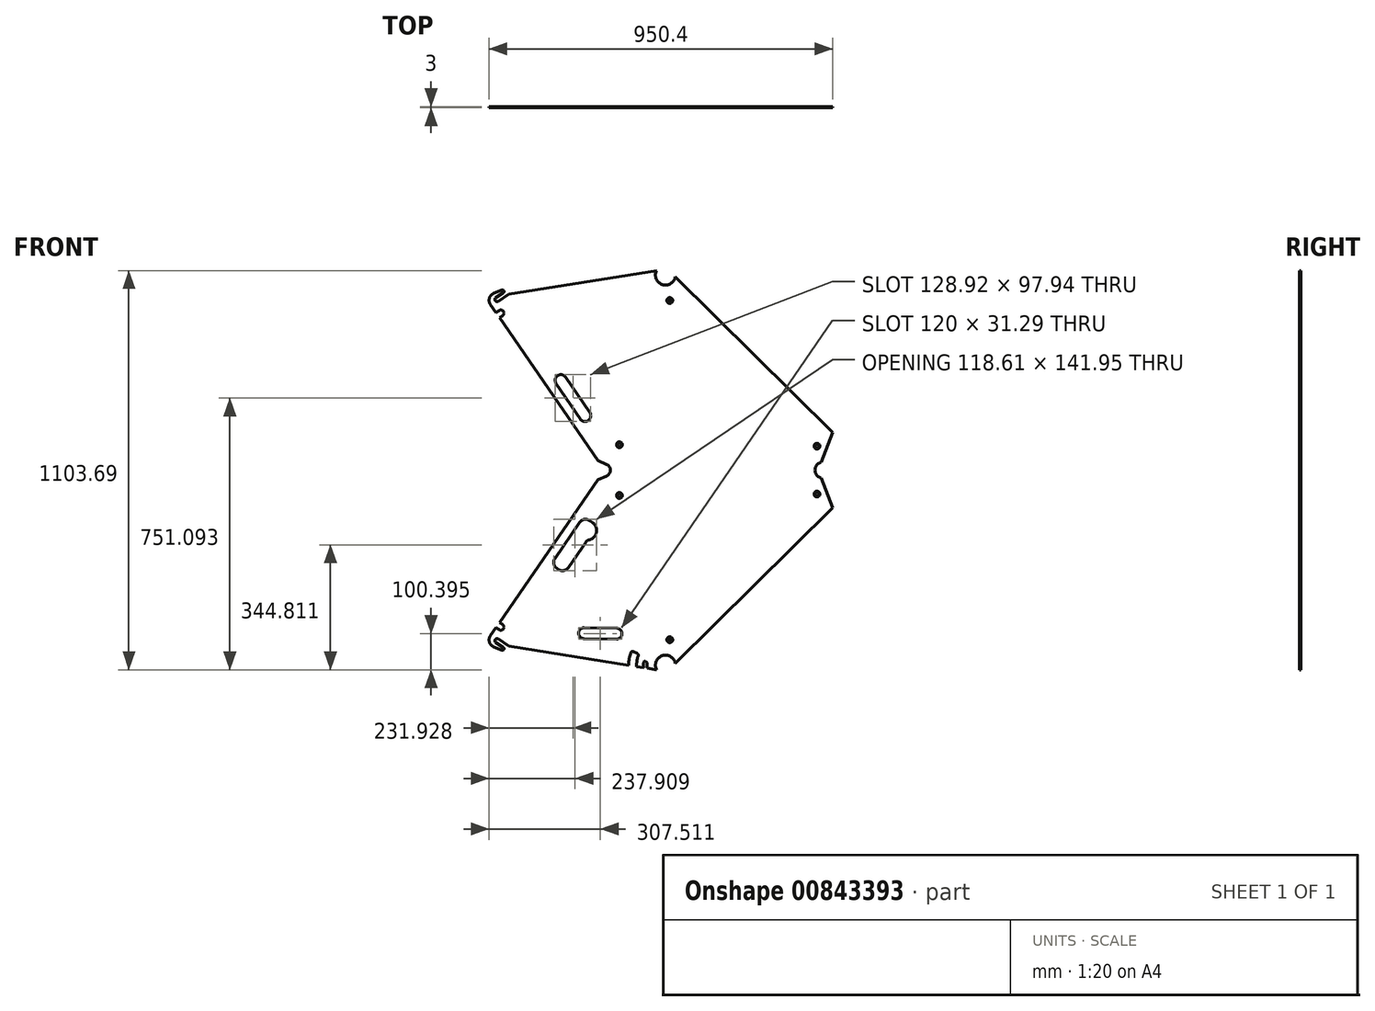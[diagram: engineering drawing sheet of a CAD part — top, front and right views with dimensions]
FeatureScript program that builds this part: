
annotation { "Feature Type Name" : "Feature", "Feature Type Description" : "" }
export const myFeature = defineFeature(function(context is Context, id is Id, definition is map)
    precondition{}
    {
        {
            var Q0;
            Q0=qCreatedBy(makeId("Front.planeOp"),FACE);
            var sketch = newSketch(context, id + "F0", { "sketchPlane" : qUnion([Q0])});
            skCircle(sketch, "E0", {"center": v(1053.9, -134.2) * mm, "radius": 17 * mm, "construction": true});
            skCircle(sketch, "E1", {"center": v(1053.9, -134.2) * mm, "radius": 21.5 * mm, "construction": true});
            skLineSegment(sketch, "E2", {"start": v(622.48, -20.32) * mm, "end": v(871.92, 345.36) * mm, "construction": true});
            skLineSegment(sketch, "E3", {"start": v(615.02, -14.4) * mm, "end": v(879.24, 372.95) * mm, "construction": true});
            skLineSegment(sketch, "E4", {"start": v(1053.9, -134.22) * mm, "end": v(865.03, 414.2) * mm, "construction": true});
            skLineSegment(sketch, "E5", {"start": v(1034.15, -125.7) * mm, "end": v(850, 409.01) * mm, "construction": true});
            skLineSegment(sketch, "E6", {"start": v(861.66, 381.3) * mm, "end": v(851.9, 409.67) * mm, "construction": true});
            skLineSegment(sketch, "E7", {"start": v(1064.21, -115.34) * mm, "end": v(880.07, 419.37) * mm, "construction": true});
            skLineSegment(sketch, "E8", {"start": v(1053.9, -134.2) * mm, "end": v(645.8, -73.78) * mm, "construction": true});
            skLineSegment(sketch, "E9", {"start": v(743.09, -99.4) * mm, "end": v(644.17, -84.76) * mm, "construction": true});
            skLineSegment(sketch, "E10", {"start": v(746.34, -77.44) * mm, "end": v(647.42, -62.8) * mm, "construction": true});
            skLineSegment(sketch, "E11", {"start": v(1035.36, -145.1) * mm, "end": v(841.66, -116.43) * mm, "construction": true});
            skLineSegment(sketch, "E12", {"start": v(1039.32, -118.4) * mm, "end": v(845.61, -89.72) * mm, "construction": true});
            skLineSegment(sketch, "E13", {"start": v(966.15, -134.86) * mm, "end": v(995.58, -139.21) * mm, "construction": true});
            skLineSegment(sketch, "E14", {"start": v(960.23, -139.03) * mm, "end": v(994.85, -144.16) * mm, "construction": true});
            skLineSegment(sketch, "E15", {"start": v(963.6, -143.58) * mm, "end": v(964.04, -140.6) * mm, "construction": true});
            skArc(sketch, "E16", {"start": v(959.64, -143) * mm, "mid": v(959.83, -143.73) * mm, "end": v(960.48, -144.13) * mm, "construction": true});
            skLineSegment(sketch, "E17", {"start": v(960.48, -144.13) * mm, "end": v(962.46, -144.42) * mm, "construction": true});
            skArc(sketch, "E18", {"start": v(962.46, -144.42) * mm, "mid": v(963.2, -144.23) * mm, "end": v(963.6, -143.58) * mm, "construction": true});
            skLineSegment(sketch, "E19", {"start": v(965.3, -133.72) * mm, "end": v(967.21, -120.86) * mm, "construction": true});
            skLineSegment(sketch, "E20", {"start": v(963, -120.24) * mm, "end": v(959.64, -143) * mm, "construction": true});
            skLineSegment(sketch, "E21", {"start": v(962.42, -124.2) * mm, "end": v(966.63, -124.82) * mm, "construction": true});
            skArc(sketch, "E22", {"start": v(965.17, -139.77) * mm, "mid": v(964.43, -139.95) * mm, "end": v(964.04, -140.6) * mm, "construction": true});
            skLineSegment(sketch, "E23", {"start": v(961.7, -129.14) * mm, "end": v(965.9, -129.76) * mm, "construction": true});
            skLineSegment(sketch, "E24", {"start": v(960.08, -126.38) * mm, "end": v(968.24, -127.58) * mm, "construction": true});
            skLineSegment(sketch, "E25", {"start": v(974.82, -141.2) * mm, "end": v(975.55, -136.25) * mm, "construction": true});
            skArc(sketch, "E26", {"start": v(965.3, -133.72) * mm, "mid": v(965.5, -134.46) * mm, "end": v(966.15, -134.86) * mm, "construction": true});
            skLineSegment(sketch, "E27", {"start": v(964.14, -119.4) * mm, "end": v(966.37, -119.73) * mm, "construction": true});
            skArc(sketch, "E28", {"start": v(964.14, -119.4) * mm, "mid": v(963.4, -119.58) * mm, "end": v(963, -120.24) * mm, "construction": true});
            skArc(sketch, "E29", {"start": v(967.21, -120.86) * mm, "mid": v(967.03, -120.12) * mm, "end": v(966.37, -119.73) * mm, "construction": true});
            skLineSegment(sketch, "E30", {"start": v(995.58, -139.21) * mm, "end": v(999.8, -144.9) * mm, "construction": true});
            skLineSegment(sketch, "E31", {"start": v(979.72, -143.94) * mm, "end": v(981.04, -135.04) * mm, "construction": true});
            skArc(sketch, "E32", {"start": v(995.7, -145.3) * mm, "mid": v(995.5, -144.55) * mm, "end": v(994.85, -144.16) * mm, "construction": true});
            skArc(sketch, "E33", {"start": v(995.25, -148.26) * mm, "mid": v(995.44, -149) * mm, "end": v(996.1, -149.4) * mm, "construction": true});
            skArc(sketch, "E34", {"start": v(998.07, -149.7) * mm, "mid": v(998.82, -149.5) * mm, "end": v(999.2, -148.85) * mm, "construction": true});
            skLineSegment(sketch, "E35", {"start": v(996.1, -149.4) * mm, "end": v(998.07, -149.7) * mm, "construction": true});
            skLineSegment(sketch, "E36", {"start": v(999.2, -148.85) * mm, "end": v(999.8, -144.9) * mm, "construction": true});
            skLineSegment(sketch, "E37", {"start": v(995.25, -148.26) * mm, "end": v(995.7, -145.3) * mm, "construction": true});
            skLineSegment(sketch, "E38", {"start": v(985.2, -142.73) * mm, "end": v(985.94, -137.79) * mm, "construction": true});
            skLineSegment(sketch, "E39", {"start": v(995.47, -146.78) * mm, "end": v(993.6, -159.38) * mm, "construction": true});
            skLineSegment(sketch, "E40", {"start": v(850, 409.01) * mm, "end": v(880.07, 419.37) * mm, "construction": true});
            skLineSegment(sketch, "E41", {"start": v(859.77, 380.65) * mm, "end": v(861.66, 381.3) * mm, "construction": true});
            skLineSegment(sketch, "E42", {"start": v(1053.9, -134.22) * mm, "end": v(1520.05, 326.73) * mm, "construction": true});
            skLineSegment(sketch, "E43", {"start": v(1081.03, -129.75) * mm, "end": v(1510.36, 294.78) * mm, "construction": true});
            skLineSegment(sketch, "E44", {"start": v(1060.7, -105.14) * mm, "end": v(1497.91, 327.2) * mm, "construction": true});
            skLineSegment(sketch, "E45", {"start": v(879.24, 372.95) * mm, "end": v(1402.67, 372.95) * mm, "construction": true});
            skLineSegment(sketch, "E46", {"start": v(901.53, 357.05) * mm, "end": v(1486.45, 357.05) * mm, "construction": true});
            skLineSegment(sketch, "E47", {"start": v(890.58, 388.85) * mm, "end": v(1474.25, 388.85) * mm, "construction": true});
            skArc(sketch, "E48", {"start": v(1486.5, 356.93) * mm, "mid": v(1487.54, 375.64) * mm, "end": v(1474.25, 388.85) * mm, "construction": true});
            skArc(sketch, "E49", {"start": v(890.58, 388.85) * mm, "mid": v(888.92, 370.5) * mm, "end": v(901.53, 357.05) * mm, "construction": true});
            skArc(sketch, "E50", {"start": v(1510.36, 294.78) * mm, "mid": v(1511.76, 313.92) * mm, "end": v(1497.91, 327.2) * mm, "construction": true});
            skArc(sketch, "E51", {"start": v(919.09, -223.5) * mm, "mid": v(918.34, -223.31) * mm, "end": v(917.6, -223.13) * mm, "construction": true});
            skFitSpline(sketch, "E52", {"points": [v(871.92, 345.36) * mm, v(875.7, 355.52) * mm, v(881.2, 370.3) * mm, v(868.26, 368.37) * mm, v(864.2, 367.77) * mm], "construction": true});
            skArc(sketch, "E53", {"start": v(591.11, -61.72) * mm, "mid": v(584.1, -63.16) * mm, "end": v(585.54, -70.17) * mm, "construction": true});
            skLineSegment(sketch, "E54", {"start": v(585.54, -70.17) * mm, "end": v(605.08, -83.05) * mm, "construction": true});
            skLineSegment(sketch, "E55", {"start": v(601.55, -93.2) * mm, "end": v(579.26, -83.87) * mm});
            skLineSegment(sketch, "E56", {"start": v(584.15, -63.19) * mm, "end": v(613.37, -82.46) * mm, "construction": true});
            skLineSegment(sketch, "E57", {"start": v(607.46, -8.63) * mm, "end": v(607.4, -8.7) * mm, "construction": true});
            skLineSegment(sketch, "E58", {"start": v(644.18, -84.66) * mm, "end": v(644.29, -83.94) * mm, "construction": true});
            skLineSegment(sketch, "E59", {"start": v(591.11, -61.72) * mm, "end": v(620.67, -81.2) * mm});
            skLineSegment(sketch, "E60", {"start": v(644.18, -84.66) * mm, "end": v(622.66, -81.47) * mm, "construction": true});
            skArc(sketch, "E61", {"start": v(644.63, -83.68) * mm, "mid": v(644.4, -83.74) * mm, "end": v(644.29, -83.94) * mm, "construction": true});
            skLineSegment(sketch, "E62", {"start": v(644.18, -84.66) * mm, "end": v(644.19, -84.63) * mm, "construction": true});
            skArc(sketch, "E63", {"start": v(601.55, -93.2) * mm, "mid": v(607.26, -91.17) * mm, "end": v(605.76, -85.3) * mm});
            skArc(sketch, "E64", {"start": v(617.78, -52.64) * mm, "mid": v(628.06, -58.54) * mm, "end": v(639.47, -61.73) * mm, "construction": true});
            skLineSegment(sketch, "E65", {"start": v(670.48, -77.43) * mm, "end": v(577.33, -63.64) * mm, "construction": true});
            skLineSegment(sketch, "E66", {"start": v(647.4, -62.9) * mm, "end": v(639.47, -61.73) * mm, "construction": true});
            skArc(sketch, "E67", {"start": v(647.3, -63.56) * mm, "mid": v(647.36, -63.78) * mm, "end": v(647.56, -63.9) * mm, "construction": true});
            skLineSegment(sketch, "E68", {"start": v(647.3, -63.56) * mm, "end": v(647.4, -62.9) * mm, "construction": true});
            skArc(sketch, "E69", {"start": v(614, -32.51) * mm, "mid": v(611.92, -43.32) * mm, "end": v(617.78, -52.64) * mm, "construction": true});
            skLineSegment(sketch, "E70", {"start": v(614, -32.51) * mm, "end": v(622.56, -20.17) * mm, "construction": true});
            skLineSegment(sketch, "E71", {"start": v(576.98, -64.11) * mm, "end": v(629.71, 4.8) * mm, "construction": true});
            skArc(sketch, "E72", {"start": v(572.75, -54.03) * mm, "mid": v(569.56, -71.65) * mm, "end": v(582.02, -84.5) * mm, "construction": true});
            skLineSegment(sketch, "E73", {"start": v(607.46, -8.63) * mm, "end": v(608.42, -9.36) * mm, "construction": true});
            skArc(sketch, "E74", {"start": v(621.55, -19.02) * mm, "mid": v(621.5, -19.24) * mm, "end": v(621.6, -19.44) * mm, "construction": true});
            skLineSegment(sketch, "E75", {"start": v(621.6, -19.44) * mm, "end": v(622.56, -20.17) * mm, "construction": true});
            skArc(sketch, "E76", {"start": v(608.42, -9.36) * mm, "mid": v(608.64, -9.42) * mm, "end": v(608.84, -9.3) * mm, "construction": true});
            skLineSegment(sketch, "E77", {"start": v(608.42, -9.36) * mm, "end": v(607.46, -8.63) * mm, "construction": true});
            skLineSegment(sketch, "E78", {"start": v(619.71, -24.29) * mm, "end": v(604.42, -12.6) * mm, "construction": true});
            skCircle(sketch, "E79", {"center": v(600.85, -74.2) * mm, "radius": 5 * mm, "construction": true});
            skLineSegment(sketch, "E80", {"start": v(621.6, -19.44) * mm, "end": v(608.42, -9.36) * mm, "construction": true});
            skLineSegment(sketch, "E81", {"start": v(841.66, -116.43) * mm, "end": v(743.09, -99.4) * mm, "construction": true});
            skLineSegment(sketch, "E82", {"start": v(746.34, -77.44) * mm, "end": v(845.61, -89.72) * mm, "construction": true});
            skEllipse(sketch, "E83", {"center": v(843.64, -103.07) * mm, "majorRadius": 13.5 * mm, "minorRadius": 8.5 * mm, "majorAxis": v(-0.15, -0.99), "construction": true});
            skCircle(sketch, "E84", {"center": v(795.03, 249.5) * mm, "radius": 9.5 * mm, "construction": true});
            skLineSegment(sketch, "E85", {"start": v(796.02, 244.3) * mm, "end": v(795.95, 244.64) * mm, "construction": true});
            skLineSegment(sketch, "E86", {"start": v(796.02, 244.3) * mm, "end": v(789.82, 248.52) * mm, "construction": true});
            skLineSegment(sketch, "E87", {"start": v(784, 242.2) * mm, "end": v(792.26, 236.56) * mm, "construction": true});
            skLineSegment(sketch, "E88", {"start": v(792.26, 236.56) * mm, "end": v(793.8, 238.84) * mm, "construction": true});
            skLineSegment(sketch, "E89", {"start": v(791.91, 236.5) * mm, "end": v(792.26, 236.56) * mm, "construction": true});
            skLineSegment(sketch, "E90", {"start": v(795.95, 244.64) * mm, "end": v(790.17, 248.58) * mm, "construction": true});
            skLineSegment(sketch, "E91", {"start": v(791.91, 236.5) * mm, "end": v(784.06, 241.85) * mm, "construction": true});
            skLineSegment(sketch, "E92", {"start": v(789.96, 238.43) * mm, "end": v(794.75, 245.46) * mm, "construction": true});
            skLineSegment(sketch, "E93", {"start": v(790.2, 238) * mm, "end": v(795.12, 245.2) * mm, "construction": true});
            skLineSegment(sketch, "E94", {"start": v(793.8, 238.84) * mm, "end": v(785.55, 244.47) * mm, "construction": true});
            skLineSegment(sketch, "E95", {"start": v(792.78, 239.54) * mm, "end": v(796.02, 244.3) * mm, "construction": true});
            skArc(sketch, "E96", {"start": v(962.06, -126.67) * mm, "mid": v(930.44, 82.62) * mm, "end": v(787.99, 239.18) * mm, "construction": true});
            skLineSegment(sketch, "E97", {"start": v(702.12, -93.34) * mm, "end": v(670.46, -88.65) * mm, "construction": true});
            skCircle(sketch, "E98", {"center": v(1053.9, -134.2) * mm, "radius": 94.9 * mm, "construction": true});
            skCircle(sketch, "E99", {"center": v(600.85, -74.2) * mm, "radius": 41.4 * mm, "construction": true});
            skLineSegment(sketch, "E100", {"start": v(1055.81, -39.3) * mm, "end": v(601.44, -32.8) * mm, "construction": true});
            skLineSegment(sketch, "E101", {"start": v(1469.36, 401.56) * mm, "end": v(1507.64, 416.26) * mm, "construction": true});
            skLineSegment(sketch, "E102", {"start": v(1507.64, 416.26) * mm, "end": v(1552.44, 299.56) * mm, "construction": true});
            skLineSegment(sketch, "E103", {"start": v(1552.44, 299.56) * mm, "end": v(1514.16, 284.87) * mm, "construction": true});
            skLineSegment(sketch, "E104", {"start": v(1514.16, 284.87) * mm, "end": v(1469.36, 401.56) * mm, "construction": true});
            skLineSegment(sketch, "E105", {"start": v(1516.78, 301.13) * mm, "end": v(1081.03, -129.75) * mm});
            skLineSegment(sketch, "E106", {"start": v(572.75, -54.03) * mm, "end": v(878.77, 388.85) * mm, "construction": true});
            skArc(sketch, "E107", {"start": v(1081.03, -129.75) * mm, "mid": v(1045.11, -108.17) * mm, "end": v(1029.6, -147.1) * mm});
            skLineSegment(sketch, "E108.trimOffspring", {"start": v(1029.6, -147.1) * mm, "end": v(620.67, -81.2) * mm});
            skCircle(sketch, "E109", {"center": v(926.64, 334.5) * mm, "radius": 4 * mm, "construction": true});
            skCircle(sketch, "E110", {"center": v(1472.9, 338.57) * mm, "radius": 4 * mm, "construction": true});
            skCircle(sketch, "E111", {"center": v(1065.9, -64.22) * mm, "radius": 4 * mm, "construction": true});
            skLineSegment(sketch, "E112", {"start": v(1053.9, -134.22) * mm, "end": v(1237.28, -134.22) * mm, "construction": true});
            skLineSegment(sketch, "E113", {"start": v(1053.9, -134.22) * mm, "end": v(1053.9, 23.55) * mm, "construction": true});
            skCircle(sketch, "E114", {"center": v(866.64, 414.5) * mm, "radius": 25 * mm, "construction": true});
            skCircle(sketch, "E115", {"center": v(1489.1, 401.54) * mm, "radius": 28.6 * mm, "construction": true});
            skLineSegment(sketch, "E116", {"start": v(1516.78, 301.13) * mm, "end": v(1482.36, 388.85) * mm});
            skLineSegment(sketch, "E117.trimOffspring", {"start": v(875.12, 388.85) * mm, "end": v(1482.36, 388.85) * mm});
            skCircle(sketch, "E118", {"center": v(600.85, -74.2) * mm, "radius": 312.5 * mm, "construction": true});
            skLineSegment(sketch, "E119.0", {"start": v(570.1, -52.58) * mm, "end": v(585.43, -30.4) * mm});
            skArc(sketch, "E120", {"start": v(570.1, -52.58) * mm, "mid": v(567.23, -70.4) * mm, "end": v(579.26, -83.87) * mm});
            skLineSegment(sketch, "E121.trimOffspring", {"start": v(598.5, -11.47) * mm, "end": v(875.12, 388.85) * mm});
            skArc(sketch, "E122", {"start": v(594.2, -36.46) * mm, "mid": v(610.2, -33.54) * mm, "end": v(607.28, -17.54) * mm, "construction": true});
            skLineSegment(sketch, "E123", {"start": v(600.85, -74.2) * mm, "end": v(600.85, 11.26) * mm, "construction": true});
            skLineSegment(sketch, "E124", {"start": v(594.2, -36.46) * mm, "end": v(585.43, -30.4) * mm, "construction": true});
            skLineSegment(sketch, "E125", {"start": v(607.28, -17.54) * mm, "end": v(598.5, -11.47) * mm, "construction": true});
            skLineSegment(sketch, "E126", {"start": v(598.5, -11.47) * mm, "end": v(595.1, -16.4) * mm});
            skLineSegment(sketch, "E127", {"start": v(595.1, -16.4) * mm, "end": v(603.87, -22.47) * mm});
            skArc(sketch, "E128", {"start": v(594.2, -36.46) * mm, "mid": v(606.03, -34.3) * mm, "end": v(603.87, -22.47) * mm});
            skLineSegment(sketch, "E129", {"start": v(585.43, -30.4) * mm, "end": v(594.2, -36.46) * mm});
            skLineSegment(sketch, "E130", {"start": v(584.23, -71.1) * mm, "end": v(605.76, -85.3) * mm});
            skArc(sketch, "E131", {"start": v(591.11, -61.72) * mm, "mid": v(583.83, -63.6) * mm, "end": v(584.23, -71.1) * mm});
            skSolve(sketch);
        }
        {
            var Q0;
            Q0=qSketchRegion(id+"F0",true);
            extrude(context, id + "F1", {"entities" : qUnion([Q0]), "depth" : 3 * mm, "offsetDistance" : 25 * mm});
        }
        {
            var Q0;
            Q0=makeQuery(id+"F1.opExtrude","SWEPT_FACE",FACE,{"disambiguationData":[OSD([sQuery(id+"F0.wireOp",EDGE,"E117.trimOffspring")])]});
            cPlane(context, id + "F2", {"entities" : qUnion([Q0]), "cplaneType" : CPlaneType.OFFSET, "offset" : 15.9 * mm, "width" : 150 * mm, "height" : 150 * mm});
        }
        {
            var Q0;
            Q0=makeQuery(id+"F1.opExtrude","SWEPT_BODY",BODY,{"disambiguationData":[OSD([sQuery(id+"F0.wireOp",EDGE,"E53"),sQuery(id+"F0.wireOp",EDGE,"E54"),sQuery(id+"F0.wireOp",EDGE,"E55"),sQuery(id+"F0.wireOp",EDGE,"E59"),sQuery(id+"F0.wireOp",EDGE,"c0fece56-cd10-4327-9040-2cab23e675d4"),sQuery(id+"F0.wireOp",EDGE,"E63"),sQuery(id+"F0.wireOp",EDGE,"E72"),sQuery(id+"F0.wireOp",EDGE,"PVY0APLz-6rdr-JrDk-CvCb-vWmYWycaJObT"),sQuery(id+"F0.wireOp",EDGE,"rSiPkJzu-22ck-wLmw-T34Z-YrS7vC3DeLN9"),sQuery(id+"F0.wireOp",EDGE,"E105"),sQuery(id+"F0.wireOp",EDGE,"E106"),sQuery(id+"F0.wireOp",EDGE,"E107"),sQuery(id+"F0.wireOp",EDGE,"E108.trimOffspring")])]});
            var Q1;
            Q1=qCreatedBy(id+"F2.planeOp",FACE);
            mirror(context, id + "F3", {"entities" : qUnion([Q0]), "mirrorPlane" : qUnion([Q1])});
        }
        {
            var Q0;
            Q0=makeQuery(id+"F1.opExtrude","CAP_FACE",FACE,{"disambiguationData":[OSD([sQuery(id+"F0.wireOp",EDGE,"E53"),sQuery(id+"F0.wireOp",EDGE,"E54"),sQuery(id+"F0.wireOp",EDGE,"E55"),sQuery(id+"F0.wireOp",EDGE,"E59"),sQuery(id+"F0.wireOp",EDGE,"c0fece56-cd10-4327-9040-2cab23e675d4"),sQuery(id+"F0.wireOp",EDGE,"E63"),sQuery(id+"F0.wireOp",EDGE,"E72"),sQuery(id+"F0.wireOp",EDGE,"PVY0APLz-6rdr-JrDk-CvCb-vWmYWycaJObT"),sQuery(id+"F0.wireOp",EDGE,"rSiPkJzu-22ck-wLmw-T34Z-YrS7vC3DeLN9"),sQuery(id+"F0.wireOp",EDGE,"E105"),sQuery(id+"F0.wireOp",EDGE,"E106"),sQuery(id+"F0.wireOp",EDGE,"E107"),sQuery(id+"F0.wireOp",EDGE,"E108.trimOffspring")])],"isStart":false});
            var sketch = newSketch(context, id + "F4", { "sketchPlane" : qUnion([Q0])});
            skArc(sketch, "E132", {"start": v(1484.73, 426.68) * mm, "mid": v(1467.24, 404.75) * mm, "end": v(1484.73, 382.81) * mm});
            skArc(sketch, "E133", {"start": v(891.59, 388.85) * mm, "mid": v(901.78, 404.75) * mm, "end": v(891.59, 420.65) * mm});
            skLineSegment(sketch, "E134", {"start": v(884.28, 404.75) * mm, "end": v(1489.74, 404.75) * mm, "construction": true});
            skLineSegment(sketch, "E135", {"start": v(891.59, 420.65) * mm, "end": v(867.46, 431.74) * mm});
            skLineSegment(sketch, "E136", {"start": v(891.59, 388.85) * mm, "end": v(867.46, 377.75) * mm});
            skLineSegment(sketch, "E137.0", {"start": v(1516.78, 508.37) * mm, "end": v(1482.36, 420.65) * mm, "construction": true});
            skLineSegment(sketch, "E138", {"start": v(1482.36, 388.85) * mm, "end": v(1516.78, 301.13) * mm, "construction": true});
            skLineSegment(sketch, "E139", {"start": v(891.59, 420.65) * mm, "end": v(1473.82, 420.65) * mm});
            skLineSegment(sketch, "E140", {"start": v(891.59, 388.85) * mm, "end": v(1473.82, 388.85) * mm});
            skSolve(sketch);
        }
        {
            var Q0;
            Q0=qSketchRegion(id+"F4",true);
            var Q1;
            Q1=makeQuery(id+"F3.opPattern","COPY",FACE,{"derivedFrom":makeQuery(id+"F1.opExtrude","CAP_FACE",FACE,{"disambiguationData":[OSD([sQuery(id+"F0.wireOp",EDGE,"E53"),sQuery(id+"F0.wireOp",EDGE,"E54"),sQuery(id+"F0.wireOp",EDGE,"E55"),sQuery(id+"F0.wireOp",EDGE,"E59"),sQuery(id+"F0.wireOp",EDGE,"c0fece56-cd10-4327-9040-2cab23e675d4"),sQuery(id+"F0.wireOp",EDGE,"E63"),sQuery(id+"F0.wireOp",EDGE,"E72"),sQuery(id+"F0.wireOp",EDGE,"PVY0APLz-6rdr-JrDk-CvCb-vWmYWycaJObT"),sQuery(id+"F0.wireOp",EDGE,"rSiPkJzu-22ck-wLmw-T34Z-YrS7vC3DeLN9"),sQuery(id+"F0.wireOp",EDGE,"E105"),sQuery(id+"F0.wireOp",EDGE,"E106"),sQuery(id+"F0.wireOp",EDGE,"E107"),sQuery(id+"F0.wireOp",EDGE,"E108.trimOffspring")])],"isStart":true}),"instanceName":"1"});
            extrude(context, id + "F5", {"entities" : qUnion([Q0]), "operationType" : NewBodyOperationType.ADD, "endBound" : BoundingType.UP_TO_SURFACE, "oppositeDirection" : true, "depth" : 65 * mm, "endBoundEntityFace" : qUnion([Q1]), "offsetDistance" : 25 * mm});
        }
        {
            var Q0;
            {var subQ0=makeQuery(id+"F1.opExtrude","CAP_FACE",FACE,{"disambiguationData":[OSD([sQuery(id+"F0.wireOp",EDGE,"E53"),sQuery(id+"F0.wireOp",EDGE,"E54"),sQuery(id+"F0.wireOp",EDGE,"E55"),sQuery(id+"F0.wireOp",EDGE,"E59"),sQuery(id+"F0.wireOp",EDGE,"E63"),sQuery(id+"F0.wireOp",EDGE,"E72"),sQuery(id+"F0.wireOp",EDGE,"E105"),sQuery(id+"F0.wireOp",EDGE,"E106"),sQuery(id+"F0.wireOp",EDGE,"E107"),sQuery(id+"F0.wireOp",EDGE,"E108.trimOffspring"),sQuery(id+"F0.wireOp",EDGE,"E109"),sQuery(id+"F0.wireOp",EDGE,"E110"),sQuery(id+"F0.wireOp",EDGE,"E111"),sQuery(id+"F0.wireOp",EDGE,"E116"),sQuery(id+"F0.wireOp",EDGE,"E117.trimOffspring")])],"isStart":false});Q0=makeQuery(id+"F5.boolean.opBoolean","MERGE",FACE,{"derivedFrom":[subQ0,makeQuery(id+"F3.opPattern","COPY",FACE,{"derivedFrom":subQ0,"instanceName":"1"}),makeQuery(id+"F5.opExtrude","CAP_FACE",FACE,{"disambiguationData":[OSD([sQuery(id+"F4.wireOp",EDGE,"E132"),sQuery(id+"F4.wireOp",EDGE,"E133"),sQuery(id+"F4.wireOp",EDGE,"E139"),sQuery(id+"F4.wireOp",EDGE,"E140")])],"isStart":true})]});}
            var sketch = newSketch(context, id + "F6", { "sketchPlane" : qUnion([Q0])});
            skLineSegment(sketch, "E141.0", {"start": v(891.59, 420.65) * mm, "end": v(867.46, 431.74) * mm});
            skLineSegment(sketch, "E141.1", {"start": v(891.59, 388.85) * mm, "end": v(867.46, 377.75) * mm});
            skArc(sketch, "E142.0", {"start": v(891.59, 388.85) * mm, "mid": v(901.78, 404.75) * mm, "end": v(891.59, 420.65) * mm});
            skLineSegment(sketch, "E143", {"start": v(867.46, 431.74) * mm, "end": v(867.46, 377.75) * mm});
            skArc(sketch, "E144.0", {"start": v(1484.73, 426.68) * mm, "mid": v(1467.24, 404.75) * mm, "end": v(1484.73, 382.81) * mm});
            skLineSegment(sketch, "E145", {"start": v(1484.73, 426.68) * mm, "end": v(1484.73, 382.81) * mm});
            skSolve(sketch);
        }
        {
            var Q0;
            Q0=qSketchRegion(id+"F6",true);
            extrude(context, id + "F7", {"entities" : qUnion([Q0]), "operationType" : NewBodyOperationType.REMOVE, "oppositeDirection" : true, "depth" : 25 * mm, "offsetDistance" : 25 * mm});
        }
        {
            var Q0;
            {var subQ0=makeQuery(id+"F1.opExtrude","CAP_FACE",FACE,{"disambiguationData":[OSD([sQuery(id+"F0.wireOp",EDGE,"E53"),sQuery(id+"F0.wireOp",EDGE,"E54"),sQuery(id+"F0.wireOp",EDGE,"E55"),sQuery(id+"F0.wireOp",EDGE,"E59"),sQuery(id+"F0.wireOp",EDGE,"E63"),sQuery(id+"F0.wireOp",EDGE,"E72"),sQuery(id+"F0.wireOp",EDGE,"PVY0APLz-6rdr-JrDk-CvCb-vWmYWycaJObT"),sQuery(id+"F0.wireOp",EDGE,"rSiPkJzu-22ck-wLmw-T34Z-YrS7vC3DeLN9"),sQuery(id+"F0.wireOp",EDGE,"E105"),sQuery(id+"F0.wireOp",EDGE,"E106"),sQuery(id+"F0.wireOp",EDGE,"E107"),sQuery(id+"F0.wireOp",EDGE,"E108.trimOffspring"),sQuery(id+"F0.wireOp",EDGE,"E109"),sQuery(id+"F0.wireOp",EDGE,"E110"),sQuery(id+"F0.wireOp",EDGE,"E111")])],"isStart":false});Q0=makeQuery(id+"F5.boolean.opBoolean","MERGE",FACE,{"derivedFrom":[subQ0,makeQuery(id+"F3.opPattern","COPY",FACE,{"derivedFrom":subQ0,"instanceName":"1"}),makeQuery(id+"F5.opExtrude","CAP_FACE",FACE,{"disambiguationData":[OSD([sQuery(id+"F4.wireOp",EDGE,"yLFeXnhX-FHJ1-lWFD-LUYU-IVhkZNTNpous"),sQuery(id+"F4.wireOp",EDGE,"25Roz2r3-I6Ic-58va-7k2N-V37a2FIcnueW"),sQuery(id+"F4.wireOp",EDGE,"Mdtmx1y3-Aq5y-VBCD-G2xE-9g1DUSUnupkp"),sQuery(id+"F4.wireOp",EDGE,"31XSQ7MP-bYWI-LpWw-hrBR-gacfVsKKRKhD")])],"isStart":true})]});}
            var sketch = newSketch(context, id + "F8", { "sketchPlane" : qUnion([Q0])});
            skLineSegment(sketch, "E146.bottom", {"start": v(829.1, -31.06) * mm, "end": v(919.1, -32.35) * mm});
            skLineSegment(sketch, "E146.top", {"start": v(828.68, -61.06) * mm, "end": v(918.68, -62.35) * mm});
            skArc(sketch, "E147", {"start": v(829.1, -31.06) * mm, "mid": v(813.9, -45.85) * mm, "end": v(828.68, -61.06) * mm});
            skArc(sketch, "E148", {"start": v(918.68, -62.35) * mm, "mid": v(933.89, -47.56) * mm, "end": v(919.1, -32.35) * mm});
            skCircle(sketch, "E149", {"center": v(1053.9, -134.22) * mm, "radius": 101.64 * mm, "construction": true});
            skPoint(sketch, "E150.0", {"position": v(1035.36, -145.1) * mm});
            skLineSegment(sketch, "E151.0", {"start": v(1035.36, -145.1) * mm, "end": v(841.66, -116.43) * mm, "construction": true});
            skPoint(sketch, "E152", {"position": v(952.27, -132.8) * mm});
            skCircle(sketch, "E153", {"center": v(1053.9, -134.22) * mm, "radius": 79.64 * mm, "construction": true});
            skPoint(sketch, "E154", {"position": v(1003.7, -140.42) * mm});
            skCircle(sketch, "E155", {"center": v(1053.9, -134.22) * mm, "radius": 50.57 * mm, "construction": true});
            skCircle(sketch, "E156", {"center": v(1053.9, -134.22) * mm, "radius": 60.57 * mm, "construction": true});
            skArc(sketch, "E157", {"start": v(958.14, -100.13) * mm, "mid": v(953.7, -117.13) * mm, "end": v(952.26, -134.64) * mm});
            skArc(sketch, "E158", {"start": v(978.53, -108.48) * mm, "mid": v(975.03, -123.14) * mm, "end": v(974.36, -138.2) * mm});
            skArc(sketch, "E159", {"start": v(964.95, -97.27) * mm, "mid": v(960.92, -97.2) * mm, "end": v(958.14, -100.13) * mm});
            skLineSegment(sketch, "E160", {"start": v(964.95, -97.27) * mm, "end": v(975.9, -102.33) * mm});
            skArc(sketch, "E161", {"start": v(978.53, -108.48) * mm, "mid": v(978.4, -104.9) * mm, "end": v(975.9, -102.33) * mm});
            skLineSegment(sketch, "E162", {"start": v(952.26, -134.64) * mm, "end": v(974.36, -138.2) * mm});
            skArc(sketch, "E163", {"start": v(993.88, -126.05) * mm, "mid": v(993.33, -133.68) * mm, "end": v(993.74, -141.32) * mm});
            skArc(sketch, "E164", {"start": v(1003.55, -129.43) * mm, "mid": v(1003.37, -136.22) * mm, "end": v(1004.1, -142.99) * mm});
            skLineSegment(sketch, "E165", {"start": v(998.61, -124.02) * mm, "end": v(1002.33, -126.71) * mm});
            skPoint(sketch, "E166.visualSharp", {"position": v(994.74, -121.22) * mm});
            skArc(sketch, "E166.filletArc", {"start": v(998.61, -124.02) * mm, "mid": v(995.67, -123.7) * mm, "end": v(993.88, -126.05) * mm});
            skPoint(sketch, "E167.visualSharp", {"position": v(1003.74, -127.74) * mm});
            skArc(sketch, "E167.filletArc", {"start": v(1003.55, -129.43) * mm, "mid": v(1003.3, -127.9) * mm, "end": v(1002.33, -126.71) * mm});
            skLineSegment(sketch, "E168", {"start": v(993.74, -141.32) * mm, "end": v(1004.1, -142.99) * mm});
            skSolve(sketch);
        }
        {
            var Q0;
            Q0=qSketchRegion(id+"F8",true);
            extrude(context, id + "F9", {"entities" : qUnion([Q0]), "operationType" : NewBodyOperationType.REMOVE, "oppositeDirection" : true, "depth" : 25 * mm, "offsetDistance" : 25 * mm});
        }
        {
            var Q0;
            {var subQ6=sQuery(id+"F4.wireOp",EDGE,"E136");Q0=makeQuery(id+"F4.imprint","IMPRINT",FACE,{"disambiguationData":[TD([[makeQuery(id+"F4.imprint","IMPRINT",EDGE,{"derivedFrom":subQ6}),1.0]])]});}
            var sketch = newSketch(context, id + "F10", { "sketchPlane" : qUnion([Q0])});
            skLineSegment(sketch, "E169", {"start": v(748.46, 160.82) * mm, "end": v(816.08, 259.96) * mm});
            skLineSegment(sketch, "E170", {"start": v(843.88, 265.2) * mm, "end": v(852.14, 259.57) * mm});
            skLineSegment(sketch, "E171", {"start": v(757.84, 130.21) * mm, "end": v(753.71, 133.03) * mm});
            skCircle(sketch, "E172.0", {"center": v(600.85, -74.2) * mm, "radius": 312.5 * mm, "construction": true});
            skLineSegment(sketch, "E172.1", {"start": v(622.48, -20.32) * mm, "end": v(871.92, 345.36) * mm, "construction": true});
            skLineSegment(sketch, "E173.0", {"start": v(884.28, 404.75) * mm, "end": v(1489.74, 404.75) * mm, "construction": true});
            skCircle(sketch, "E174.MirrorC", {"center": v(600.85, 883.7) * mm, "radius": 312.5 * mm, "construction": true});
            skLineSegment(sketch, "E175.MirrorCS", {"start": v(622.48, 829.82) * mm, "end": v(871.92, 464.13) * mm, "construction": true});
            skLineSegment(sketch, "E176", {"start": v(818.34, 546.24) * mm, "end": v(751.84, 643.72) * mm});
            skLineSegment(sketch, "E177", {"start": v(756.04, 665.95) * mm, "end": v(756.04, 665.95) * mm});
            skLineSegment(sketch, "E178", {"start": v(778.28, 661.75) * mm, "end": v(844.77, 564.27) * mm});
            skLineSegment(sketch, "E179", {"start": v(840.57, 542.04) * mm, "end": v(840.57, 542.04) * mm});
            skLineSegment(sketch, "E180.0", {"start": v(797.53, 236.3) * mm, "end": v(785.55, 244.47) * mm, "construction": true});
            skLineSegment(sketch, "E181.MirrorCS", {"start": v(797.53, 573.2) * mm, "end": v(785.55, 565.03) * mm, "construction": true});
            skLineSegment(sketch, "E182", {"start": v(797.53, 573.2) * mm, "end": v(768.19, 553.19) * mm, "construction": true});
            skPoint(sketch, "E183.orphan", {"position": v(793.8, 570.66) * mm});
            skPoint(sketch, "E184.orphan", {"position": v(793.8, 238.84) * mm});
            skLineSegment(sketch, "E185", {"start": v(797.53, 236.3) * mm, "end": v(778.55, 249.24) * mm, "construction": true});
            skPoint(sketch, "E186.visualSharp", {"position": v(827.35, 276.48) * mm});
            skArc(sketch, "E186.filletArc", {"start": v(843.88, 265.2) * mm, "mid": v(828.9, 268.34) * mm, "end": v(816.08, 259.96) * mm});
            skPoint(sketch, "E187.visualSharp", {"position": v(872.79, 245.49) * mm});
            skArc(sketch, "E187.filletArc", {"start": v(842.48, 211.69) * mm, "mid": v(863.19, 232.43) * mm, "end": v(852.14, 259.57) * mm});
            skPoint(sketch, "E188.visualSharp", {"position": v(737.2, 144.3) * mm});
            skArc(sketch, "E188.filletArc", {"start": v(748.46, 160.82) * mm, "mid": v(745.33, 145.84) * mm, "end": v(753.71, 133.03) * mm});
            skPoint(sketch, "E189.visualSharp", {"position": v(782.63, 113.3) * mm});
            skArc(sketch, "E189.filletArc", {"start": v(757.84, 130.21) * mm, "mid": v(772.83, 127.08) * mm, "end": v(785.64, 135.47) * mm});
            skPoint(sketch, "E190.visualSharp", {"position": v(742.83, 656.94) * mm});
            skArc(sketch, "E190.filletArc", {"start": v(756.04, 665.95) * mm, "mid": v(749.34, 655.7) * mm, "end": v(751.84, 643.72) * mm});
            skPoint(sketch, "E191.visualSharp", {"position": v(769.26, 674.97) * mm});
            skArc(sketch, "E191.filletArc", {"start": v(778.28, 661.75) * mm, "mid": v(768.03, 668.46) * mm, "end": v(756.04, 665.95) * mm});
            skPoint(sketch, "E192.visualSharp", {"position": v(853.79, 551.05) * mm});
            skArc(sketch, "E192.filletArc", {"start": v(840.57, 542.04) * mm, "mid": v(847.28, 552.28) * mm, "end": v(844.77, 564.27) * mm});
            skPoint(sketch, "E193.visualSharp", {"position": v(827.35, 533.02) * mm});
            skArc(sketch, "E193.filletArc", {"start": v(818.34, 546.24) * mm, "mid": v(828.58, 539.53) * mm, "end": v(840.57, 542.04) * mm});
            skLineSegment(sketch, "E194", {"start": v(785.64, 135.47) * mm, "end": v(833.6, 205.8) * mm});
            skArc(sketch, "E195", {"start": v(842.48, 211.69) * mm, "mid": v(837.47, 209.6) * mm, "end": v(833.6, 205.8) * mm});
            skSolve(sketch);
        }
        {
            var Q0;
            Q0 = qSketchRegion(id + "F10", true);
            extrude(context, id + "F11", {"entities" : qUnion([Q0]), "operationType" : NewBodyOperationType.REMOVE, "endBound" : BoundingType.THROUGH_ALL, "oppositeDirection" : true, "depth" : 25 * mm, "offsetDistance" : 25 * mm});
        }
        {
            var Q0;
            {var subQ7=sQuery(id+"F4.wireOp",EDGE,"E136");Q0=makeQuery(id+"F4.imprint","IMPRINT",FACE,{"disambiguationData":[TD([[makeQuery(id+"F4.imprint","IMPRINT",EDGE,{"derivedFrom":subQ7}),1.0]])]});}
            var Q1;
            {var subQ7=sQuery(id+"F4.wireOp",EDGE,"E136");Q1=makeQuery(id+"F4.imprint","IMPRINT",FACE,{"disambiguationData":[TD([[makeQuery(id+"F4.imprint","IMPRINT",EDGE,{"derivedFrom":subQ7}),1.0]])]});}
            var sketch = newSketch(context, id + "F12", { "sketchPlane" : qUnion([Q0, Q1])});
            skPoint(sketch, "E196.0", {"position": v(926.64, 334.5) * mm});
            skPoint(sketch, "E196.1", {"position": v(1472.9, 338.57) * mm});
            skPoint(sketch, "E196.2", {"position": v(1065.9, -64.22) * mm});
            skPoint(sketch, "E197.MirrorP", {"position": v(926.64, 475) * mm});
            skPoint(sketch, "E198.MirrorP", {"position": v(1472.9, 470.93) * mm});
            skPoint(sketch, "E199.MirrorP", {"position": v(1065.9, 873.72) * mm});
            skSolve(sketch);
        }
        {
            var Q0;
            Q0=sQuery(id+"F12.wireOp",VERTEX,"E199.MirrorP");
            var Q1;
            Q1=sQuery(id+"F12.wireOp",VERTEX,"E197.MirrorP");
            var Q2;
            Q2=sQuery(id+"F12.wireOp",VERTEX,"E198.MirrorP");
            var Q3;
            Q3=sQuery(id+"F0.wireOp",VERTEX,"E109.center");
            var Q4;
            Q4=sQuery(id+"F0.wireOp",VERTEX,"E110.center");
            var Q5;
            Q5=sQuery(id+"F0.wireOp",VERTEX,"E111.center");
            var Q6;
            Q6=sQuery(id+"F12.wireOp",VERTEX,"E196.2");
            var Q7;
            Q7=sQuery(id+"F12.wireOp",VERTEX,"E196.0");
            var Q8;
            Q8=sQuery(id+"F12.wireOp",VERTEX,"E196.1");
            var Q9;
            Q9=makeQuery(id+"F1.opExtrude","SWEPT_BODY",BODY,{"disambiguationData":[OSD([sQuery(id+"F0.wireOp",EDGE,"E53"),sQuery(id+"F0.wireOp",EDGE,"E54"),sQuery(id+"F0.wireOp",EDGE,"E55"),sQuery(id+"F0.wireOp",EDGE,"E59"),sQuery(id+"F0.wireOp",EDGE,"E63"),sQuery(id+"F0.wireOp",EDGE,"E105"),sQuery(id+"F0.wireOp",EDGE,"E107"),sQuery(id+"F0.wireOp",EDGE,"E108.trimOffspring"),sQuery(id+"F0.wireOp",EDGE,"E116"),sQuery(id+"F0.wireOp",EDGE,"E117.trimOffspring"),sQuery(id+"F0.wireOp",EDGE,"E119.0"),sQuery(id+"F0.wireOp",EDGE,"E120"),sQuery(id+"F0.wireOp",EDGE,"E121.trimOffspring"),sQuery(id+"F0.wireOp",EDGE,"E122"),sQuery(id+"F0.wireOp",EDGE,"E124"),sQuery(id+"F0.wireOp",EDGE,"E125")])]});
            hole(context, id + "F13", {"style" : HoleStyle.C_SINK, "endStyle" : HoleEndStyle.THROUGH, "holeDiameter" : 8 * mm, "cSinkDiameter" : 16 * mm, "cSinkAngle" : 90 * degree, "majorDiameter" : 5 * mm, "isTappedThrough" : true, "tappedDepth" : 12 * mm, "tapClearance" : 3, "locations" : qUnion([Q0, Q1, Q2, Q3, Q4, Q5, Q6, Q7, Q8]), "scope" : qUnion([Q9])});
        }
    });
